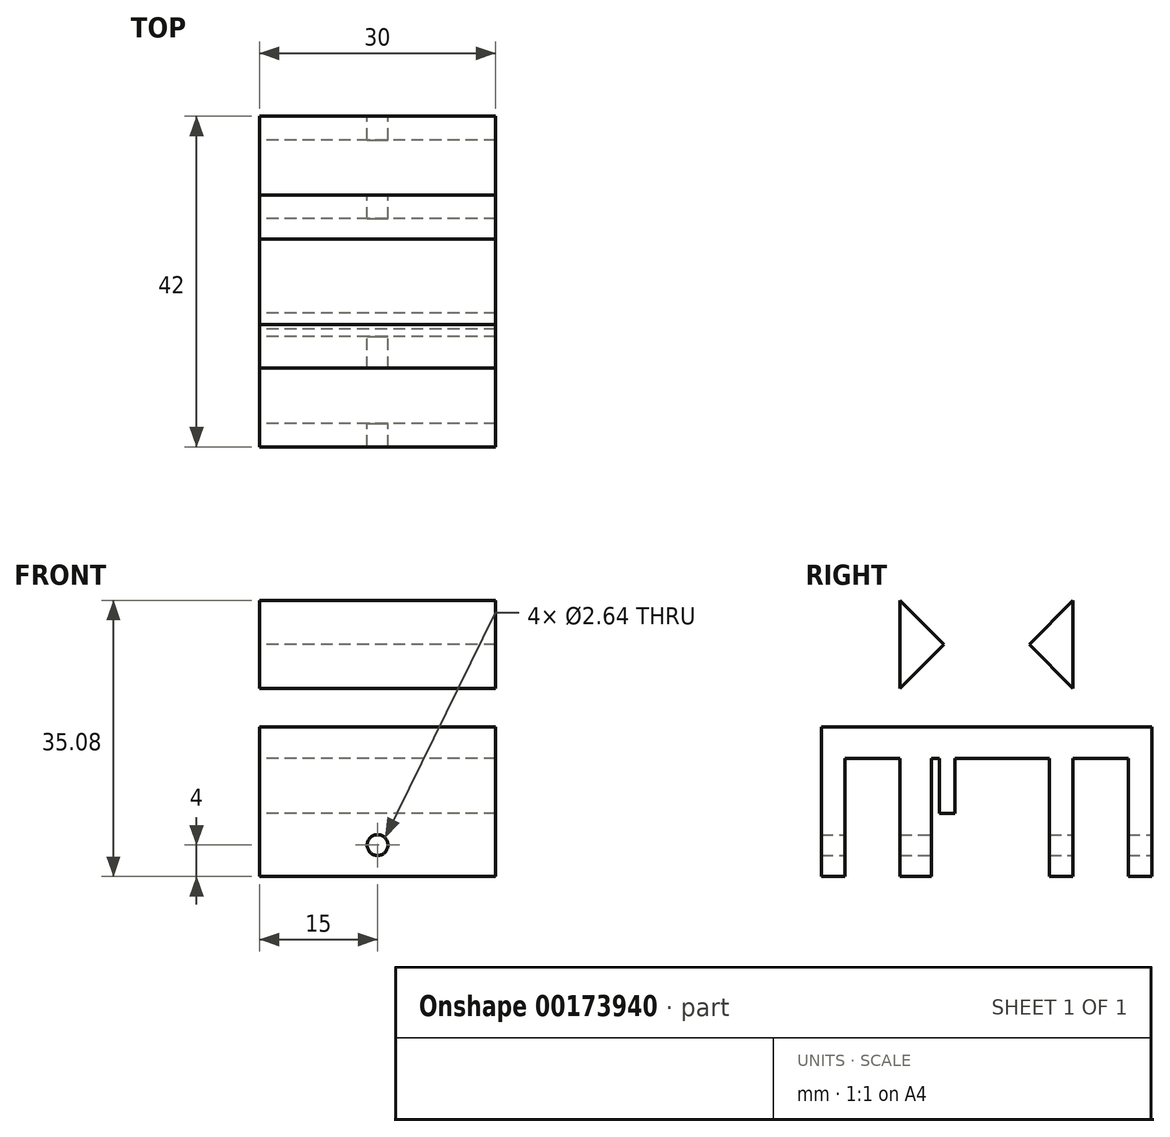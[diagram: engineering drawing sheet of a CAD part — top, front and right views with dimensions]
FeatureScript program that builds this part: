
annotation { "Feature Type Name" : "Feature", "Feature Type Description" : "" }
export const myFeature = defineFeature(function(context is Context, id is Id, definition is map)
    precondition{}
    {
        {
            var Q0;
            Q0=qCreatedBy(makeId("Right.planeOp"),FACE);
            var sketch = newSketch(context, id + "F0", { "sketchPlane" : qUnion([Q0])});
            skLineSegment(sketch, "E0.bottom", {"start": v(-21, 0) * mm, "end": v(21, 0) * mm});
            skLineSegment(sketch, "E0.top", {"start": v(-21, 4) * mm, "end": v(21, 4) * mm});
            skLineSegment(sketch, "E0.left", {"start": v(-21, 0) * mm, "end": v(-21, 4) * mm});
            skLineSegment(sketch, "E0.right", {"start": v(21, 0) * mm, "end": v(21, 4) * mm});
            skLineSegment(sketch, "E1.bottom", {"start": v(21, 4) * mm, "end": v(11, 4) * mm});
            skLineSegment(sketch, "E1.top", {"start": v(21, 25) * mm, "end": v(11, 25) * mm});
            skLineSegment(sketch, "E1.left", {"start": v(21, 4) * mm, "end": v(21, 25) * mm});
            skLineSegment(sketch, "E1.right", {"start": v(11, 4) * mm, "end": v(11, 25) * mm});
            skLineSegment(sketch, "E2", {"start": v(0, 0) * mm, "end": v(0, 12.87) * mm});
            skLineSegment(sketch, "E3.MirrorCS", {"start": v(-11, 4) * mm, "end": v(-11, 25) * mm});
            skLineSegment(sketch, "E4.MirrorCS", {"start": v(-21, 25) * mm, "end": v(-11, 25) * mm});
            skLineSegment(sketch, "E5.MirrorCS", {"start": v(-21, 4) * mm, "end": v(-21, 25) * mm});
            skLineSegment(sketch, "E6.MirrorCS", {"start": v(-21, 4) * mm, "end": v(-11, 4) * mm});
            skLineSegment(sketch, "E7", {"start": v(11, 20.08) * mm, "end": v(5.42, 14.5) * mm});
            skPoint(sketch, "E7.endSnap0", {"position": v(11, 14.5) * mm});
            skLineSegment(sketch, "E8", {"start": v(5.42, 14.5) * mm, "end": v(11, 8.92) * mm});
            skLineSegment(sketch, "E9.MirrorCS", {"start": v(-5.42, 14.5) * mm, "end": v(-11, 8.92) * mm});
            skLineSegment(sketch, "E10.MirrorCS", {"start": v(-11, 20.08) * mm, "end": v(-5.42, 14.5) * mm});
            skLineSegment(sketch, "E11", {"start": v(-13, 25) * mm, "end": v(-21, 4) * mm});
            skLineSegment(sketch, "E12", {"start": v(13, 25) * mm, "end": v(21, 4) * mm});
            skSolve(sketch);
        }
        {
            var Q0;
            {var subQ0=sQuery(id+"F0.wireOp",EDGE,"E7");Q0=makeQuery(id+"F0.imprint","IMPRINT",FACE,{"disambiguationData":[TD([[makeQuery(id+"F0.imprint","IMPRINT",EDGE,{"derivedFrom":subQ0}),1.0]])]});}
            var Q1;
            {var subQ0=sQuery(id+"F0.wireOp",EDGE,"E9.MirrorCS");Q1=makeQuery(id+"F0.imprint","IMPRINT",FACE,{"disambiguationData":[TD([[makeQuery(id+"F0.imprint","IMPRINT",EDGE,{"derivedFrom":subQ0}),-1.0]])]});}
            var Q2;
            {var subQ5=sQuery(id+"F0.wireOp",EDGE,"E0.left");Q2=makeQuery(id+"F0.imprint","IMPRINT",FACE,{"disambiguationData":[TD([[makeQuery(id+"F0.imprint","IMPRINT",EDGE,{"derivedFrom":subQ5}),-1.0]])]});}
            var Q3;
            {var subQ1=sQuery(id+"F0.wireOp",EDGE,"E0.right");Q3=makeQuery(id+"F0.imprint","IMPRINT",FACE,{"disambiguationData":[TD([[makeQuery(id+"F0.imprint","IMPRINT",EDGE,{"derivedFrom":subQ1}),1.0]])]});}
            var Q4;
            {var subQ4=sQuery(id+"F0.wireOp",EDGE,"E1.bottom");Q4=makeQuery(id+"F0.imprint","IMPRINT",FACE,{"disambiguationData":[TD([[makeQuery(id+"F0.imprint","IMPRINT",EDGE,{"derivedFrom":subQ4}),-1.0]])]});}
            var Q5;
            {var subQ0=sQuery(id+"F0.wireOp",EDGE,"E6.MirrorCS");Q5=makeQuery(id+"F0.imprint","IMPRINT",FACE,{"disambiguationData":[TD([[makeQuery(id+"F0.imprint","IMPRINT",EDGE,{"derivedFrom":subQ0}),1.0]])]});}
            extrude(context, id + "F1", {"entities" : qUnion([Q0, Q1, Q2, Q3, Q4, Q5]), "depth" : 30 * mm});
        }
        {
            var Q0;
            Q0=qCreatedBy(makeId("Right.planeOp"),FACE);
            var sketch = newSketch(context, id + "F2", { "sketchPlane" : qUnion([Q0])});
            skLineSegment(sketch, "E13.bottom", {"start": v(-11, 0) * mm, "end": v(-7, 0) * mm});
            skLineSegment(sketch, "E13.top", {"start": v(-11, -15) * mm, "end": v(-7, -15) * mm});
            skLineSegment(sketch, "E13.left", {"start": v(-7, 0) * mm, "end": v(-7, -15) * mm});
            skLineSegment(sketch, "E13.right", {"start": v(-11, 0) * mm, "end": v(-11, -15) * mm});
            skLineSegment(sketch, "E14.bottom", {"start": v(8, 0) * mm, "end": v(11, 0) * mm});
            skLineSegment(sketch, "E14.top", {"start": v(8, -15) * mm, "end": v(11, -15) * mm});
            skLineSegment(sketch, "E14.left", {"start": v(8, 0) * mm, "end": v(8, -15) * mm});
            skLineSegment(sketch, "E14.right", {"start": v(11, 0) * mm, "end": v(11, -15) * mm});
            skLineSegment(sketch, "E15.bottom", {"start": v(18, 0) * mm, "end": v(21, 0) * mm});
            skLineSegment(sketch, "E15.top", {"start": v(18, -15) * mm, "end": v(21, -15) * mm});
            skLineSegment(sketch, "E15.left", {"start": v(21, 0) * mm, "end": v(21, -15) * mm});
            skLineSegment(sketch, "E15.right", {"start": v(18, 0) * mm, "end": v(18, -15) * mm});
            skLineSegment(sketch, "E16.bottom", {"start": v(-21, 0) * mm, "end": v(-18, 0) * mm});
            skLineSegment(sketch, "E16.top", {"start": v(-21, -15) * mm, "end": v(-18, -15) * mm});
            skLineSegment(sketch, "E16.left", {"start": v(-21, 0) * mm, "end": v(-21, -15) * mm});
            skLineSegment(sketch, "E16.right", {"start": v(-18, 0) * mm, "end": v(-18, -15) * mm});
            skLineSegment(sketch, "E17.bottom", {"start": v(-6, 0) * mm, "end": v(0, 0) * mm});
            skLineSegment(sketch, "E17.top", {"start": v(-6, -7) * mm, "end": v(-4, -7) * mm});
            skLineSegment(sketch, "E17.left", {"start": v(-6, 0) * mm, "end": v(-6, -7) * mm});
            skLineSegment(sketch, "E17.right", {"start": v(-4, 0) * mm, "end": v(-4, -7) * mm});
            skLineSegment(sketch, "E18", {"start": v(6, 0) * mm, "end": v(6, -15.6) * mm});
            skSolve(sketch);
        }
        {
            var Q0;
            Q0=makeQuery(id+"F2.imprint","IMPRINT",FACE,{"disambiguationData":[TD([[makeQuery(id+"F2.imprint","IMPRINT",EDGE,{"derivedFrom":sQuery(id+"F2.wireOp",EDGE,"E16.bottom")}),-1.0]])]});
            var Q1;
            Q1=makeQuery(id+"F2.imprint","IMPRINT",FACE,{"disambiguationData":[TD([[makeQuery(id+"F2.imprint","IMPRINT",EDGE,{"derivedFrom":sQuery(id+"F2.wireOp",EDGE,"E14.bottom")}),-1.0]])]});
            var Q2;
            Q2=makeQuery(id+"F2.imprint","IMPRINT",FACE,{"disambiguationData":[TD([[makeQuery(id+"F2.imprint","IMPRINT",EDGE,{"derivedFrom":sQuery(id+"F2.wireOp",EDGE,"E15.bottom")}),-1.0]])]});
            var Q3;
            Q3=makeQuery(id+"F1.opExtrude","CAP_FACE",FACE,{"disambiguationData":[OSD([sQuery(id+"F0.wireOp",EDGE,"E0.bottom"),sQuery(id+"F0.wireOp",EDGE,"E0.top"),sQuery(id+"F0.wireOp",EDGE,"E0.left"),sQuery(id+"F0.wireOp",EDGE,"E0.right"),sQuery(id+"F0.wireOp",EDGE,"E1.top"),sQuery(id+"F0.wireOp",EDGE,"E1.left"),sQuery(id+"F0.wireOp",EDGE,"E1.right"),sQuery(id+"F0.wireOp",EDGE,"E4.MirrorCS"),sQuery(id+"F0.wireOp",EDGE,"E5.MirrorCS"),sQuery(id+"F0.wireOp",EDGE,"E3.MirrorCS"),sQuery(id+"F0.wireOp",EDGE,"E7"),sQuery(id+"F0.wireOp",EDGE,"E8"),sQuery(id+"F0.wireOp",EDGE,"E9.MirrorCS"),sQuery(id+"F0.wireOp",EDGE,"E10.MirrorCS")])],"isStart":false});
            extrude(context, id + "F3", {"entities" : qUnion([Q0, Q1, Q2]), "operationType" : NewBodyOperationType.ADD, "endBound" : BoundingType.UP_TO_SURFACE, "endBoundEntityFace" : qUnion([Q3]), "depth" : 10 * mm});
        }
        {
            var Q0;
            Q0=makeQuery(id+"F2.imprint","IMPRINT",FACE,{"disambiguationData":[TD([[makeQuery(id+"F2.imprint","IMPRINT",EDGE,{"derivedFrom":sQuery(id+"F2.wireOp",EDGE,"E13.bottom")}),-1.0]])]});
            var Q1;
            Q1=makeQuery(id+"F1.opExtrude","CAP_FACE",FACE,{"disambiguationData":[OSD([sQuery(id+"F0.wireOp",EDGE,"E0.bottom"),sQuery(id+"F0.wireOp",EDGE,"E0.top"),sQuery(id+"F0.wireOp",EDGE,"E0.left"),sQuery(id+"F0.wireOp",EDGE,"E0.right"),sQuery(id+"F0.wireOp",EDGE,"E1.top"),sQuery(id+"F0.wireOp",EDGE,"E1.left"),sQuery(id+"F0.wireOp",EDGE,"E1.right"),sQuery(id+"F0.wireOp",EDGE,"E4.MirrorCS"),sQuery(id+"F0.wireOp",EDGE,"E5.MirrorCS"),sQuery(id+"F0.wireOp",EDGE,"E3.MirrorCS"),sQuery(id+"F0.wireOp",EDGE,"E7"),sQuery(id+"F0.wireOp",EDGE,"E8"),sQuery(id+"F0.wireOp",EDGE,"E9.MirrorCS"),sQuery(id+"F0.wireOp",EDGE,"E10.MirrorCS")])],"isStart":false});
            extrude(context, id + "F4", {"entities" : qUnion([Q0]), "operationType" : NewBodyOperationType.ADD, "endBound" : BoundingType.UP_TO_SURFACE, "endBoundEntityFace" : qUnion([Q1]), "depth" : 25 * mm});
        }
        {
            var Q0;
            Q0=makeQuery(id+"F2.imprint","IMPRINT",FACE,{"disambiguationData":[TD([[makeQuery(id+"F2.imprint","IMPRINT",EDGE,{"derivedFrom":sQuery(id+"F2.wireOp",EDGE,"E17.top")}),1.0]])]});
            var Q1;
            Q1=makeQuery(id+"F1.opExtrude","CAP_FACE",FACE,{"disambiguationData":[OSD([sQuery(id+"F0.wireOp",EDGE,"E0.bottom"),sQuery(id+"F0.wireOp",EDGE,"E0.top"),sQuery(id+"F0.wireOp",EDGE,"E0.left"),sQuery(id+"F0.wireOp",EDGE,"E0.right"),sQuery(id+"F0.wireOp",EDGE,"E1.top"),sQuery(id+"F0.wireOp",EDGE,"E1.left"),sQuery(id+"F0.wireOp",EDGE,"E1.right"),sQuery(id+"F0.wireOp",EDGE,"E4.MirrorCS"),sQuery(id+"F0.wireOp",EDGE,"E5.MirrorCS"),sQuery(id+"F0.wireOp",EDGE,"E3.MirrorCS"),sQuery(id+"F0.wireOp",EDGE,"E7"),sQuery(id+"F0.wireOp",EDGE,"E8"),sQuery(id+"F0.wireOp",EDGE,"E9.MirrorCS"),sQuery(id+"F0.wireOp",EDGE,"E10.MirrorCS")])],"isStart":false});
            extrude(context, id + "F5", {"entities" : qUnion([Q0]), "operationType" : NewBodyOperationType.ADD, "endBound" : BoundingType.UP_TO_SURFACE, "endBoundEntityFace" : qUnion([Q1]), "depth" : 25 * mm});
        }
        {
            var Q0;
            Q0=makeQuery(id+"F3.boolean.opBoolean","MERGE",FACE,{"derivedFrom":[makeQuery(id+"F1.opExtrude","SWEPT_FACE",FACE,{"disambiguationData":[OSD([sQuery(id+"F0.wireOp",EDGE,"E0.right")])]}),makeQuery(id+"F3.opExtrude","SWEPT_FACE",FACE,{"disambiguationData":[OSD([sQuery(id+"F2.wireOp",EDGE,"E15.left")])]})]});
            var sketch = newSketch(context, id + "F6", { "sketchPlane" : qUnion([Q0])});
            skLineSegment(sketch, "E19", {"start": v(0, -11) * mm, "end": v(-30, -11) * mm});
            skLineSegment(sketch, "E20", {"start": v(-15, -15) * mm, "end": v(-15, -6.7) * mm});
            skPoint(sketch, "E21", {"position": v(-15, -11) * mm});
            skSolve(sketch);
        }
        {
            var Q0;
            Q0=sQuery(id+"F6.wireOp",VERTEX,"E21");
            var Q1;
            Q1=makeQuery(id+"F1.opExtrude","SWEPT_BODY",BODY,{"disambiguationData":[OSD([sQuery(id+"F0.wireOp",EDGE,"E0.bottom"),sQuery(id+"F0.wireOp",EDGE,"E0.top"),sQuery(id+"F0.wireOp",EDGE,"E0.left"),sQuery(id+"F0.wireOp",EDGE,"E0.right"),sQuery(id+"F0.wireOp",EDGE,"E1.top"),sQuery(id+"F0.wireOp",EDGE,"E1.left"),sQuery(id+"F0.wireOp",EDGE,"E1.right"),sQuery(id+"F0.wireOp",EDGE,"E4.MirrorCS"),sQuery(id+"F0.wireOp",EDGE,"E5.MirrorCS"),sQuery(id+"F0.wireOp",EDGE,"E3.MirrorCS"),sQuery(id+"F0.wireOp",EDGE,"E7"),sQuery(id+"F0.wireOp",EDGE,"E8"),sQuery(id+"F0.wireOp",EDGE,"E9.MirrorCS"),sQuery(id+"F0.wireOp",EDGE,"E10.MirrorCS")])]});
            hole(context, id + "F7", {"style" : HoleStyle.SIMPLE, "endStyle" : HoleEndStyle.THROUGH, "standardTappedOrClearance" : lookupTablePath({ "standard" : "ANSI", "fit" : "Close", "size" : "#3", "type" : "Clearance" }), "standardBlindInLast" : lookupTablePath({ "fit" : "Close", "standard" : "ANSI", "size" : "#3", "type" : "Clearance" }), "holeDiameter" : 2.64 * mm, "locations" : qUnion([Q0]), "scope" : qUnion([Q1]), "isTappedThrough" : true});
        }
    });
